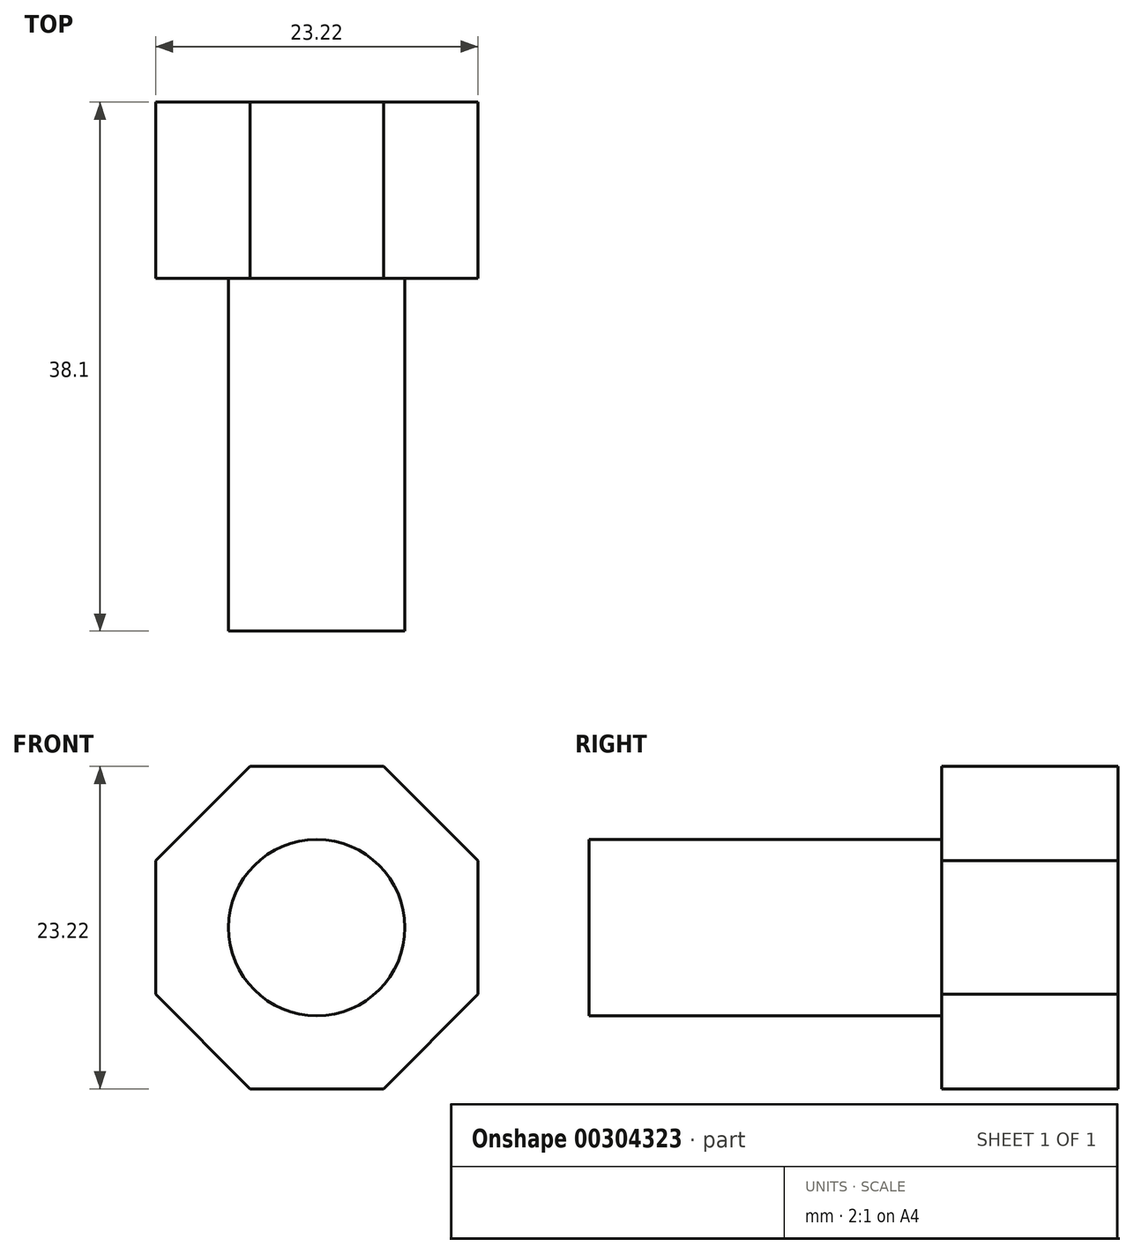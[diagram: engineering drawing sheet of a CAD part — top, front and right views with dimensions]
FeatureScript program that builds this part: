
annotation { "Feature Type Name" : "Feature", "Feature Type Description" : "" }
export const myFeature = defineFeature(function(context is Context, id is Id, definition is map)
    precondition{}
    {
        {
            var Q0;
            Q0=qCreatedBy(makeId("Front.planeOp"),FACE);
            var sketch = newSketch(context, id + "F0", { "sketchPlane" : qUnion([Q0])});
            skCircle(sketch, "E0", {"center": v(0, 0) * mm, "radius": 6.35 * mm});
            skSolve(sketch);
        }
        {
            var Q0;
            Q0=makeQuery(id+"F0.imprint","IMPRINT",FACE,{"disambiguationData":[TD([[makeQuery(id+"F0.imprint","IMPRINT",EDGE,{"derivedFrom":sQuery(id+"F0.wireOp",EDGE,"E0")}),1.0]])]});
            extrude(context, id + "F1", {"entities" : qUnion([Q0]), "depth" : 38.1 * mm});
        }
        {
            var Q0;
            Q0=makeQuery(id+"F1.opExtrude","CAP_FACE",FACE,{"disambiguationData":[OSD([sQuery(id+"F0.wireOp",EDGE,"E0")])],"isStart":true});
            var sketch = newSketch(context, id + "F2", { "sketchPlane" : qUnion([Q0])});
            skCircle(sketch, "E1.cCircle", {"center": v(0, 0) * mm, "radius": 11.61 * mm, "construction": true});
            skLineSegment(sketch, "E1.0", {"start": v(4.8, -11.61) * mm, "end": v(-4.8, -11.61) * mm});
            skLineSegment(sketch, "E1.1", {"start": v(-4.8, -11.61) * mm, "end": v(-11.61, -4.8) * mm});
            skLineSegment(sketch, "E1.2", {"start": v(-11.61, -4.8) * mm, "end": v(-11.61, 4.8) * mm});
            skLineSegment(sketch, "E1.3", {"start": v(-11.61, 4.8) * mm, "end": v(-4.8, 11.61) * mm});
            skLineSegment(sketch, "E1.4", {"start": v(-4.8, 11.61) * mm, "end": v(4.8, 11.61) * mm});
            skLineSegment(sketch, "E1.5", {"start": v(4.8, 11.61) * mm, "end": v(11.61, 4.8) * mm});
            skLineSegment(sketch, "E1.6", {"start": v(11.61, 4.8) * mm, "end": v(11.61, -4.8) * mm});
            skLineSegment(sketch, "E1.7", {"start": v(11.61, -4.8) * mm, "end": v(4.8, -11.61) * mm});
            skPoint(sketch, "E1.0.midPoint", {"position": v(0, -11.61) * mm});
            skSolve(sketch);
        }
        {
            var Q0;
            Q0=makeQuery(id+"F2.imprint","IMPRINT",FACE,{"disambiguationData":[TD([[makeQuery(id+"F2.imprint","IMPRINT",EDGE,{"derivedFrom":sQuery(id+"F2.wireOp",EDGE,"E1.0")}),-1.0]])]});
            extrude(context, id + "F3", {"entities" : qUnion([Q0]), "operationType" : NewBodyOperationType.ADD, "oppositeDirection" : true, "depth" : 12.7 * mm});
        }
    });
